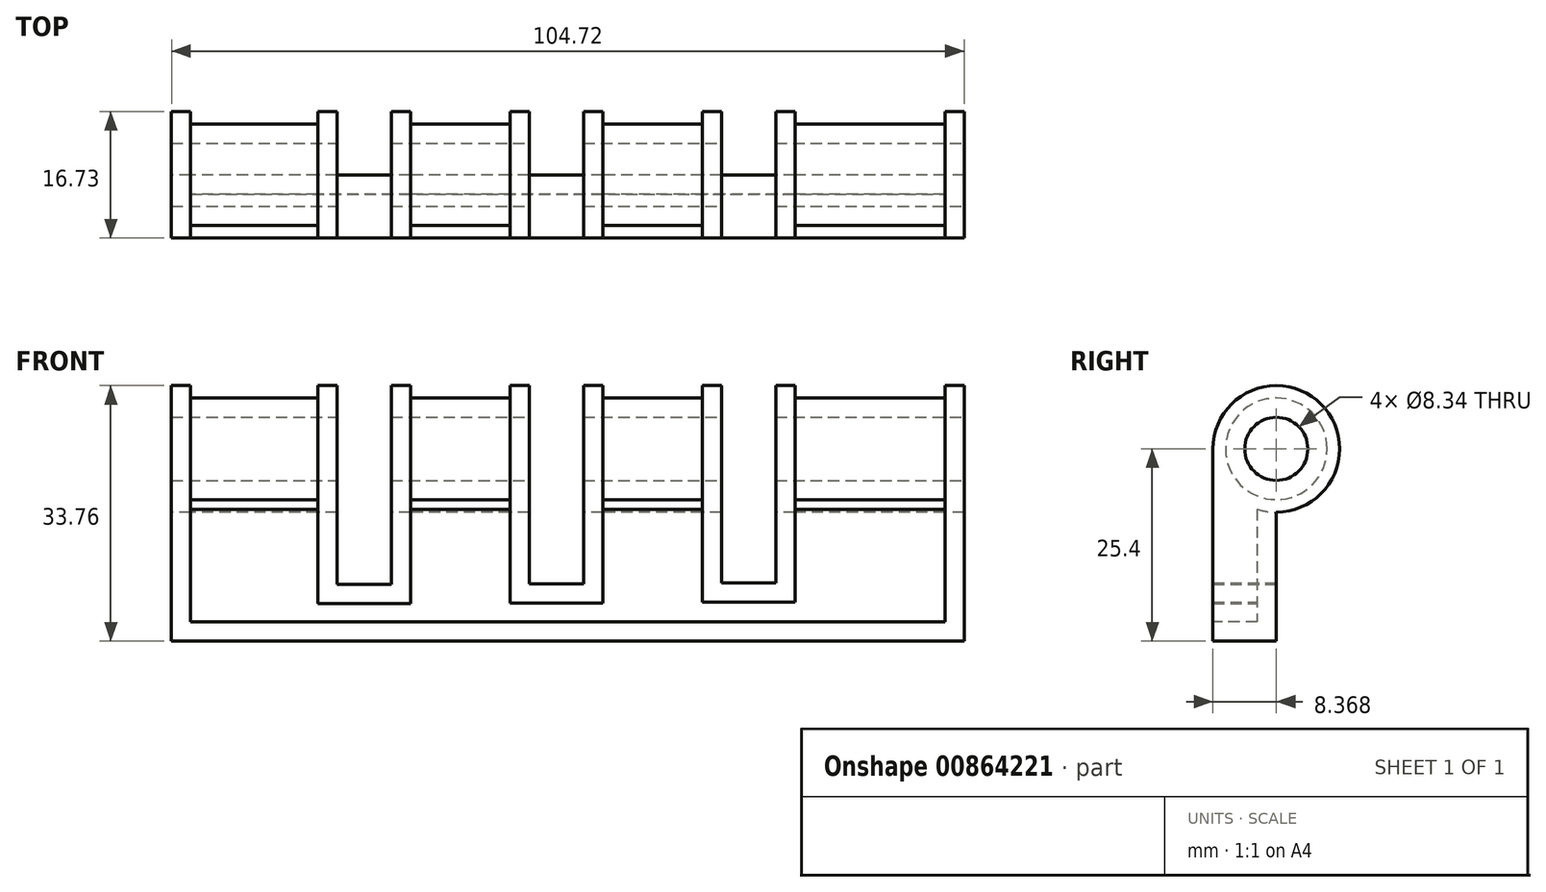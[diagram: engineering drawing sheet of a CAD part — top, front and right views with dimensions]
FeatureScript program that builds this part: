
annotation { "Feature Type Name" : "Feature", "Feature Type Description" : "" }
export const myFeature = defineFeature(function(context is Context, id is Id, definition is map)
    precondition{}
    {
        {
            var Q0;
            Q0=qCreatedBy(makeId("Top.planeOp"),FACE);
            var sketch = newSketch(context, id + "F0", { "sketchPlane" : qUnion([Q0])});
            skLineSegment(sketch, "E0.bottom", {"start": v(-49.24, -40.21) * mm, "end": v(55.48, -40.21) * mm});
            skLineSegment(sketch, "E0.top", {"start": v(-49.24, -48.58) * mm, "end": v(55.48, -48.58) * mm});
            skLineSegment(sketch, "E0.left", {"start": v(-49.24, -40.21) * mm, "end": v(-49.24, -48.58) * mm});
            skLineSegment(sketch, "E0.right", {"start": v(55.48, -40.21) * mm, "end": v(55.48, -48.58) * mm});
            skSolve(sketch);
        }
        {
            var Q0;
            Q0 = qSketchRegion(id + "F0", true);
            extrude(context, id + "F1", {"entities" : qUnion([Q0]), "depth" : 25.4 * mm, "offsetDistance" : 25.4 * mm});
        }
        {
            var Q0;
            Q0=makeQuery(id+"F1.opExtrude","CAP_FACE",FACE,{"disambiguationData":[OSD([sQuery(id+"F0.wireOp",EDGE,"E0.bottom"),sQuery(id+"F0.wireOp",EDGE,"E0.top"),sQuery(id+"F0.wireOp",EDGE,"E0.left"),sQuery(id+"F0.wireOp",EDGE,"E0.right")])],"isStart":false});
            var sketch = newSketch(context, id + "F2", { "sketchPlane" : qUnion([Q0])});
            skSolve(sketch);
        }
        {
            var Q0;
            Q0=makeQuery(id+"F2.imprint","IMPRINT",FACE,{"disambiguationData":[TD([[makeQuery(id+"F2.imprint","IMPRINT",EDGE,{"derivedFrom":makeQuery(id+"F1.opExtrude","CAP_EDGE",EDGE,{"disambiguationData":[OSD([sQuery(id+"F0.wireOp",EDGE,"E0.bottom")])],"isStart":false})}),-1.0]])]});
            var Q1;
            Q1=makeQuery(id+"F1.opExtrude","CAP_EDGE",EDGE,{"disambiguationData":[OSD([sQuery(id+"F0.wireOp",EDGE,"E0.bottom")])],"isStart":false});
            revolve(context, id + "F3", {"operationType" : NewBodyOperationType.ADD, "surfaceOperationType" : NewSurfaceOperationType.NEW, "entities" : qUnion([Q0]), "axis" : qUnion([Q1]), "revolveType" : RevolveType.TWO_DIRECTIONS, "angle" : 180 * degree, "angleBack" : 180 * degree});
        }
        {
            var Q0;
            Q0=makeQuery(id+"F1.opExtrude","SWEPT_FACE",FACE,{"disambiguationData":[OSD([sQuery(id+"F0.wireOp",EDGE,"E0.bottom")])]});
            var sketch = newSketch(context, id + "F4", { "sketchPlane" : qUnion([Q0])});
            skLineSegment(sketch, "E1.bottom", {"start": v(-30.6, 45.1) * mm, "end": v(-23.42, 45.1) * mm});
            skLineSegment(sketch, "E1.top", {"start": v(-30.6, 7.66) * mm, "end": v(-23.42, 7.66) * mm});
            skLineSegment(sketch, "E1.left", {"start": v(-30.6, 45.1) * mm, "end": v(-30.6, 7.66) * mm});
            skLineSegment(sketch, "E1.right", {"start": v(-23.42, 45.1) * mm, "end": v(-23.42, 7.66) * mm});
            skLineSegment(sketch, "E2.1.0.0", {"start": v(-5.2, 45) * mm, "end": v(-5.2, 7.57) * mm});
            skLineSegment(sketch, "E2.1.0.1", {"start": v(1.98, 45) * mm, "end": v(1.98, 7.57) * mm});
            skLineSegment(sketch, "E2.1.0.2", {"start": v(-5.2, 45) * mm, "end": v(1.98, 45) * mm});
            skLineSegment(sketch, "E2.1.0.3", {"start": v(-5.2, 7.57) * mm, "end": v(1.98, 7.57) * mm});
            skLineSegment(sketch, "E2.2.0.0", {"start": v(20.2, 44.91) * mm, "end": v(20.2, 7.47) * mm});
            skLineSegment(sketch, "E2.2.0.1", {"start": v(27.38, 44.91) * mm, "end": v(27.38, 7.47) * mm});
            skLineSegment(sketch, "E2.2.0.2", {"start": v(20.2, 44.91) * mm, "end": v(27.38, 44.91) * mm});
            skLineSegment(sketch, "E2.2.0.3", {"start": v(20.2, 7.47) * mm, "end": v(27.38, 7.47) * mm});
            skLineSegment(sketch, "E2.direction1", {"start": v(-30.6, 7.66) * mm, "end": v(-5.2, 7.57) * mm, "construction": true});
            skSolve(sketch);
        }
        {
            var Q0;
            {var subQ0=sQuery(id+"F4.wireOp",EDGE,"E2.1.0.2");Q0=makeQuery(id+"F4.imprint","IMPRINT",FACE,{"disambiguationData":[TD([[makeQuery(id+"F4.imprint","IMPRINT",EDGE,{"derivedFrom":subQ0}),-1.0]])]});}
            var Q1;
            {var subQ0=sQuery(id+"F4.wireOp",EDGE,"E2.2.0.2");Q1=makeQuery(id+"F4.imprint","IMPRINT",FACE,{"disambiguationData":[TD([[makeQuery(id+"F4.imprint","IMPRINT",EDGE,{"derivedFrom":subQ0}),-1.0]])]});}
            var Q2;
            {var subQ0=sQuery(id+"F4.wireOp",EDGE,"E1.bottom");Q2=makeQuery(id+"F4.imprint","IMPRINT",FACE,{"disambiguationData":[TD([[makeQuery(id+"F4.imprint","IMPRINT",EDGE,{"derivedFrom":subQ0}),-1.0]])]});}
            var Q3;
            {var subQ0=sQuery(id+"F4.wireOp",EDGE,"E1.top");Q3=makeQuery(id+"F4.imprint","IMPRINT",FACE,{"disambiguationData":[TD([[makeQuery(id+"F4.imprint","IMPRINT",EDGE,{"derivedFrom":subQ0}),1.0]])]});}
            var Q4;
            {var subQ0=sQuery(id+"F4.wireOp",EDGE,"E2.1.0.3");Q4=makeQuery(id+"F4.imprint","IMPRINT",FACE,{"disambiguationData":[TD([[makeQuery(id+"F4.imprint","IMPRINT",EDGE,{"derivedFrom":subQ0}),1.0]])]});}
            var Q5;
            {var subQ0=sQuery(id+"F4.wireOp",EDGE,"E2.2.0.3");Q5=makeQuery(id+"F4.imprint","IMPRINT",FACE,{"disambiguationData":[TD([[makeQuery(id+"F4.imprint","IMPRINT",EDGE,{"derivedFrom":subQ0}),1.0]])]});}
            extrude(context, id + "F5", {"entities" : qUnion([Q0, Q1, Q2, Q3, Q4, Q5]), "operationType" : NewBodyOperationType.REMOVE, "endBound" : BoundingType.SYMMETRIC, "oppositeDirection" : true, "depth" : 76.2 * mm, "offsetDistance" : 25.4 * mm});
        }
        {
            var Q0;
            {var subQ0=sQuery(id+"F0.wireOp",EDGE,"E0.right");Q0=makeQuery(id+"F3.boolean.opBoolean","MERGE",FACE,{"derivedFrom":[makeQuery(id+"F1.opExtrude","SWEPT_FACE",FACE,{"disambiguationData":[OSD([subQ0])]}),makeQuery(id+"F3.opRevolve","SWEPT_FACE",FACE,{"disambiguationData":[OSD([subQ0])]})]});}
            var sketch = newSketch(context, id + "F6", { "sketchPlane" : qUnion([Q0])});
            skCircle(sketch, "E3", {"center": v(-40.21, 25.4) * mm, "radius": 4.17 * mm});
            skSolve(sketch);
        }
        {
            var Q0;
            Q0=makeQuery(id+"F6.imprint","IMPRINT",FACE,{"disambiguationData":[TD([[makeQuery(id+"F6.imprint","IMPRINT",EDGE,{"derivedFrom":sQuery(id+"F6.wireOp",EDGE,"E3")}),1.0]])]});
            extrude(context, id + "F7", {"entities" : qUnion([Q0]), "operationType" : NewBodyOperationType.REMOVE, "endBound" : BoundingType.THROUGH_ALL, "oppositeDirection" : true, "depth" : 25.4 * mm, "offsetDistance" : 25.4 * mm});
        }
        {
            var Q0;
            Q0=makeQuery(id+"F1.opExtrude","SWEPT_FACE",FACE,{"disambiguationData":[OSD([sQuery(id+"F0.wireOp",EDGE,"E0.top")])]});
            var Q1;
            {var subQ0=sQuery(id+"F0.wireOp",EDGE,"E0.top");var subQ1=sQuery(id+"F0.wireOp",EDGE,"E0.right");Q1=makeQuery(id+"F5.boolean.opBoolean","SPLIT",FACE,{"disambiguationData":[TD([makeQuery(id+"F1.opExtrude","SWEPT_FACE",FACE,{"disambiguationData":[OSD([subQ1])]})])],"derivedFrom":makeQuery(id+"F3.opRevolve","SWEPT_FACE",FACE,{"disambiguationData":[OSD([subQ0])]})});}
            var Q2;
            {var subQ0=sQuery(id+"F0.wireOp",EDGE,"E0.top");Q2=makeQuery(id+"F5.boolean.opBoolean","SPLIT",FACE,{"disambiguationData":[TD([makeQuery(id+"F5.opExtrude","SWEPT_FACE",FACE,{"disambiguationData":[OSD([sQuery(id+"F4.wireOp",EDGE,"E1.right")])]})])],"derivedFrom":makeQuery(id+"F3.opRevolve","SWEPT_FACE",FACE,{"disambiguationData":[OSD([subQ0])]})});}
            var Q3;
            {var subQ0=sQuery(id+"F0.wireOp",EDGE,"E0.top");Q3=makeQuery(id+"F5.boolean.opBoolean","SPLIT",FACE,{"disambiguationData":[TD([makeQuery(id+"F5.opExtrude","SWEPT_FACE",FACE,{"disambiguationData":[OSD([sQuery(id+"F4.wireOp",EDGE,"E2.1.0.1")])]})])],"derivedFrom":makeQuery(id+"F3.opRevolve","SWEPT_FACE",FACE,{"disambiguationData":[OSD([subQ0])]})});}
            var Q4;
            {var subQ0=sQuery(id+"F0.wireOp",EDGE,"E0.left");var subQ1=sQuery(id+"F0.wireOp",EDGE,"E0.top");Q4=makeQuery(id+"F5.boolean.opBoolean","SPLIT",FACE,{"disambiguationData":[TD([makeQuery(id+"F1.opExtrude","SWEPT_FACE",FACE,{"disambiguationData":[OSD([subQ0])]})])],"derivedFrom":makeQuery(id+"F3.opRevolve","SWEPT_FACE",FACE,{"disambiguationData":[OSD([subQ1])]})});}
            shell(context, id + "F8", {"entities" : qUnion([Q0, Q1, Q2, Q3, Q4]), "thickness" : 2.54 * mm});
        }
    });
